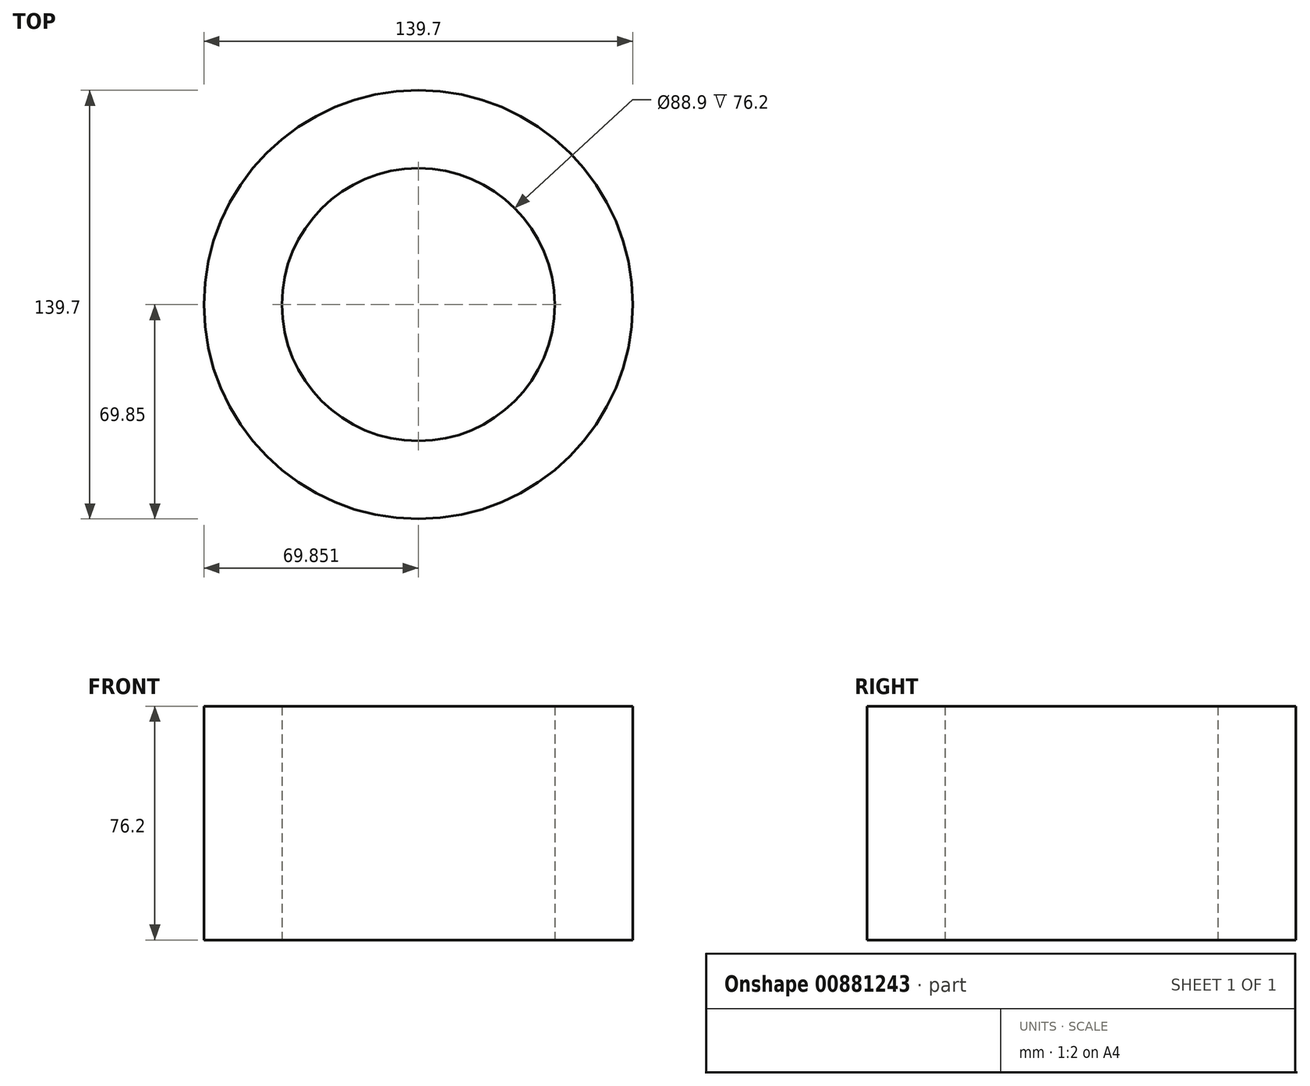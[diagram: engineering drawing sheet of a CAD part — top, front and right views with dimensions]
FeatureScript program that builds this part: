
annotation { "Feature Type Name" : "Feature", "Feature Type Description" : "" }
export const myFeature = defineFeature(function(context is Context, id is Id, definition is map)
    precondition{}
    {
        {
            var Q0;
            Q0=qCreatedBy(makeId("Top.planeOp"),FACE);
            var sketch = newSketch(context, id + "F0", { "sketchPlane" : qUnion([Q0])});
            skCircle(sketch, "E0", {"center": v(4.58, 0) * mm, "radius": 44.45 * mm});
            skCircle(sketch, "E1", {"center": v(4.58, 0) * mm, "radius": 69.85 * mm});
            skSolve(sketch);
        }
        {
            var Q0;
            Q0=qSketchRegion(id+"F0",true);
            extrude(context, id + "F1", {"entities" : qUnion([Q0]), "depth" : 76.2 * mm, "offsetDistance" : 25.4 * mm});
        }
    });
